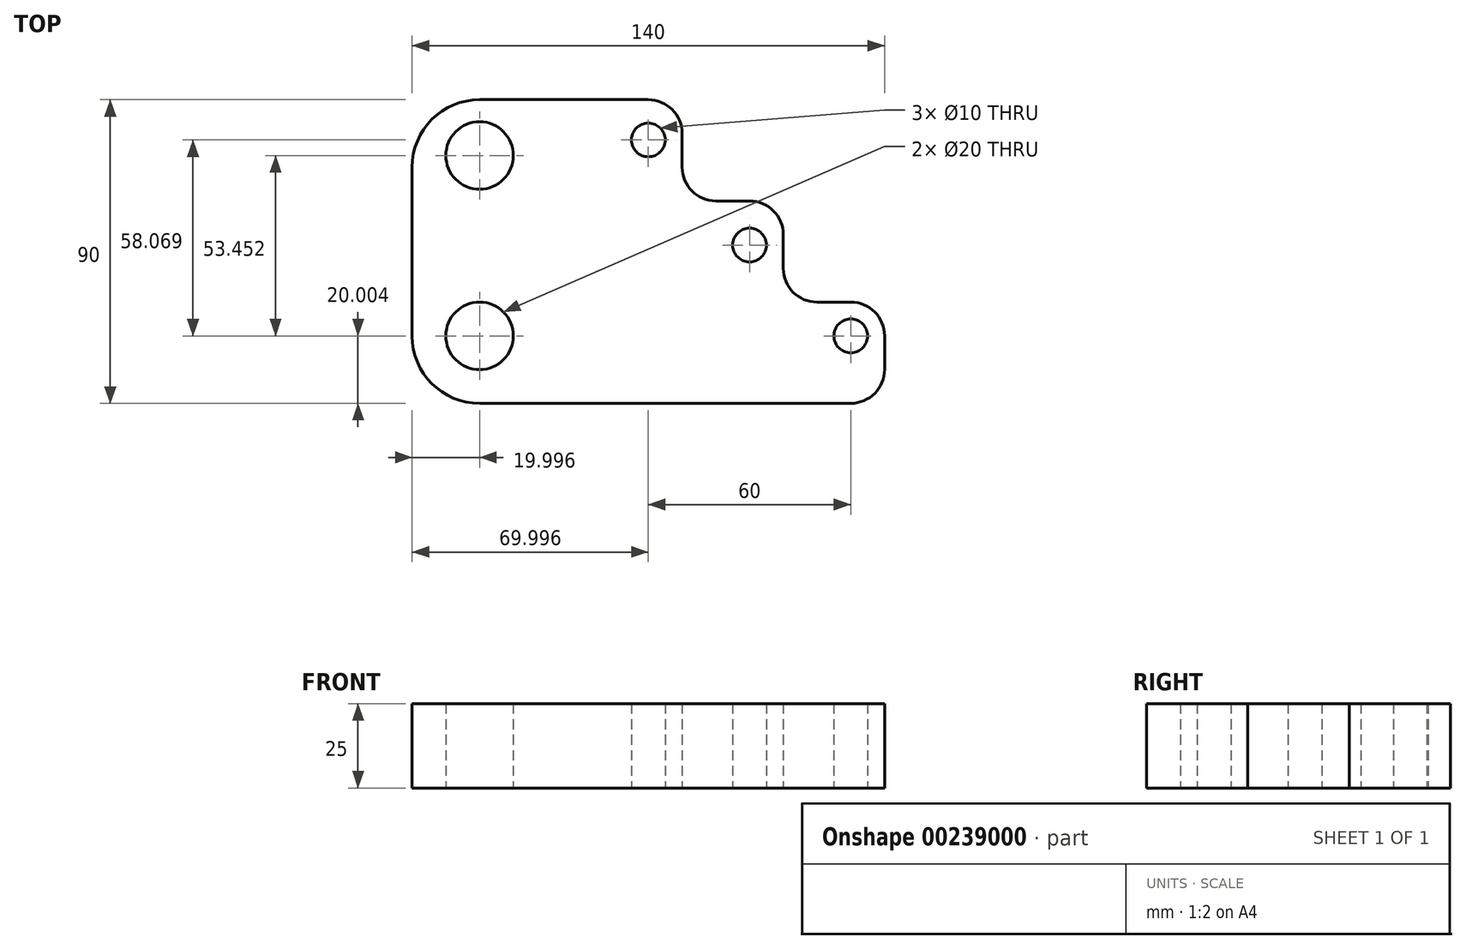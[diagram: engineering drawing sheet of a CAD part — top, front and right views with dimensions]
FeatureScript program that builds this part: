
annotation { "Feature Type Name" : "Feature", "Feature Type Description" : "" }
export const myFeature = defineFeature(function(context is Context, id is Id, definition is map)
    precondition{}
    {
        {
            var Q0;
            Q0=qCreatedBy(makeId("Top.planeOp"),FACE);
            var sketch = newSketch(context, id + "F0", { "sketchPlane" : qUnion([Q0])});
            skLineSegment(sketch, "E0", {"start": v(-60.26, -9.19) * mm, "end": v(49.74, -9.19) * mm});
            skLineSegment(sketch, "E1", {"start": v(-80.26, 10.81) * mm, "end": v(-80.26, 60.81) * mm});
            skLineSegment(sketch, "E2", {"start": v(-60.26, 80.81) * mm, "end": v(-10.26, 80.81) * mm});
            skLineSegment(sketch, "E3", {"start": v(-0.26, 60.81) * mm, "end": v(-0.26, 70.81) * mm});
            skLineSegment(sketch, "E4", {"start": v(9.74, 50.81) * mm, "end": v(19.74, 50.81) * mm});
            skLineSegment(sketch, "E5", {"start": v(29.74, 40.81) * mm, "end": v(29.74, 30.81) * mm});
            skLineSegment(sketch, "E6", {"start": v(39.74, 20.81) * mm, "end": v(49.74, 20.81) * mm});
            skLineSegment(sketch, "E7", {"start": v(59.74, 0.81) * mm, "end": v(59.74, 10.81) * mm});
            skPoint(sketch, "E8.visualSharp", {"position": v(-80.26, 80.81) * mm});
            skArc(sketch, "E8.filletArc", {"start": v(-60.26, 80.81) * mm, "mid": v(-74.4, 74.96) * mm, "end": v(-80.26, 60.81) * mm});
            skPoint(sketch, "E9.visualSharp", {"position": v(-80.26, -9.19) * mm});
            skArc(sketch, "E9.filletArc", {"start": v(-80.26, 10.81) * mm, "mid": v(-74.4, -3.33) * mm, "end": v(-60.26, -9.19) * mm});
            skPoint(sketch, "E10.visualSharp", {"position": v(-0.26, 80.81) * mm});
            skArc(sketch, "E10.filletArc", {"start": v(-0.26, 70.81) * mm, "mid": v(-3.2, 77.88) * mm, "end": v(-10.26, 80.81) * mm});
            skPoint(sketch, "E11.visualSharp", {"position": v(29.74, 50.81) * mm});
            skArc(sketch, "E11.filletArc", {"start": v(29.74, 40.81) * mm, "mid": v(26.8, 47.88) * mm, "end": v(19.74, 50.81) * mm});
            skPoint(sketch, "E12.visualSharp", {"position": v(59.74, 20.81) * mm});
            skArc(sketch, "E12.filletArc", {"start": v(59.74, 10.81) * mm, "mid": v(56.8, 17.88) * mm, "end": v(49.74, 20.81) * mm});
            skPoint(sketch, "E13.visualSharp", {"position": v(59.74, -9.19) * mm});
            skArc(sketch, "E13.filletArc", {"start": v(49.74, -9.19) * mm, "mid": v(56.8, -6.26) * mm, "end": v(59.74, 0.81) * mm});
            skPoint(sketch, "E14.visualSharp", {"position": v(-0.26, 50.81) * mm});
            skArc(sketch, "E14.filletArc", {"start": v(-0.26, 60.81) * mm, "mid": v(2.66, 53.74) * mm, "end": v(9.74, 50.81) * mm});
            skPoint(sketch, "E15.visualSharp", {"position": v(29.74, 20.81) * mm});
            skArc(sketch, "E15.filletArc", {"start": v(29.74, 30.81) * mm, "mid": v(32.66, 23.74) * mm, "end": v(39.74, 20.81) * mm});
            skCircle(sketch, "E16", {"center": v(-60.26, 64.27) * mm, "radius": 10 * mm});
            skCircle(sketch, "E17", {"center": v(-10.26, 68.88) * mm, "radius": 5 * mm});
            skCircle(sketch, "E18", {"center": v(19.74, 37.72) * mm, "radius": 5 * mm});
            skCircle(sketch, "E19", {"center": v(-60.26, 10.81) * mm, "radius": 10 * mm});
            skCircle(sketch, "E20", {"center": v(49.74, 10.81) * mm, "radius": 5 * mm});
            skSolve(sketch);
        }
        {
            var Q0;
            Q0 = qSketchRegion(id + "F0", true);
            extrude(context, id + "F1", {"entities" : qUnion([Q0]), "depth" : 25 * mm});
        }
    });
